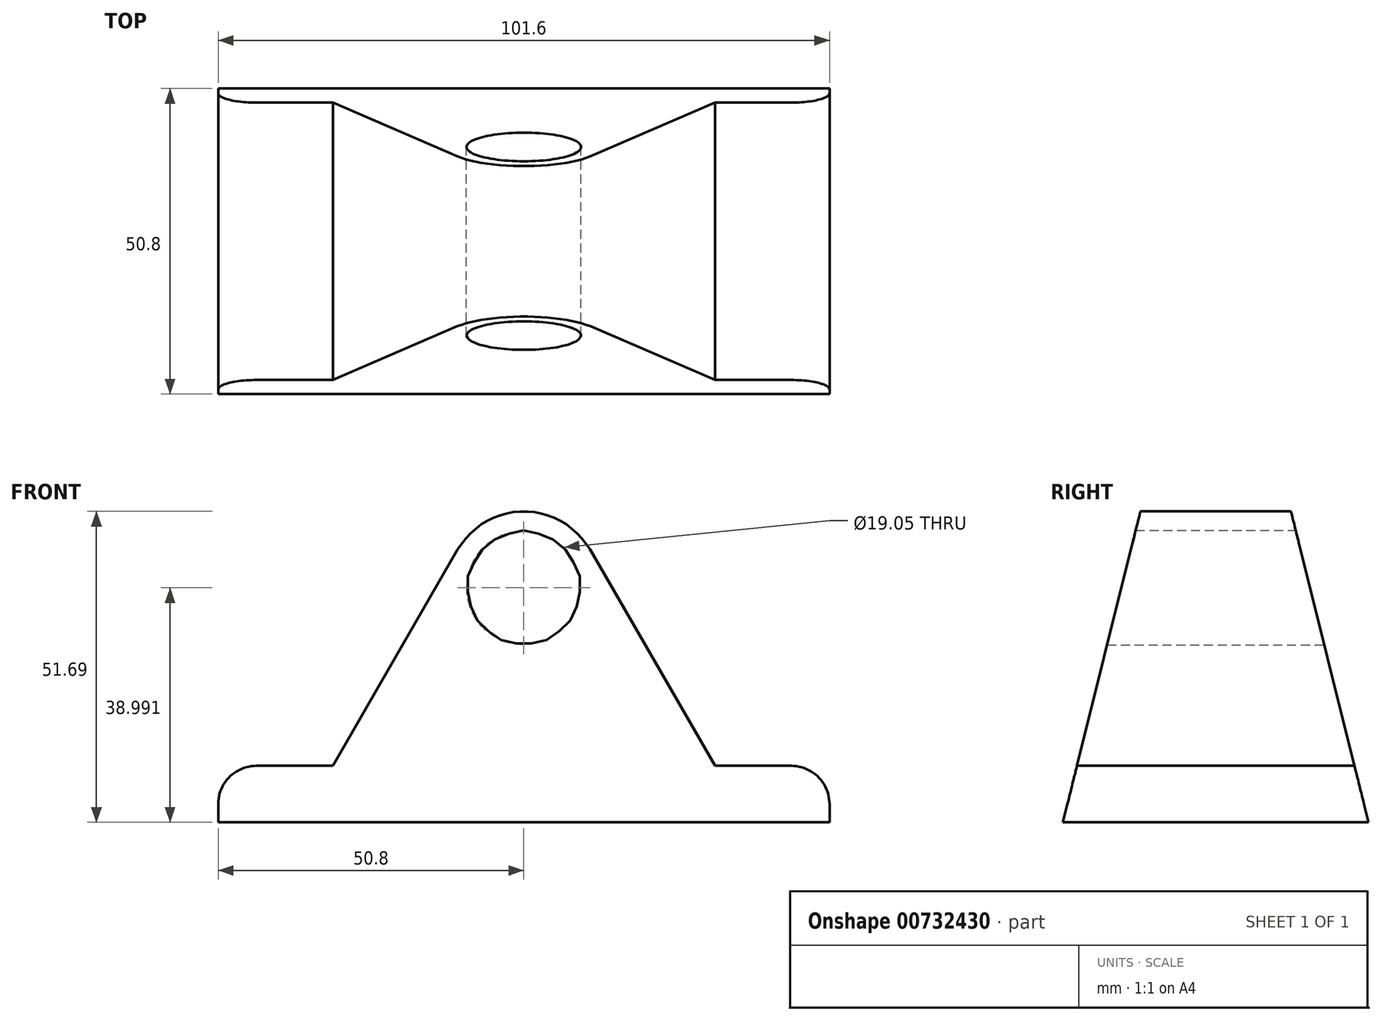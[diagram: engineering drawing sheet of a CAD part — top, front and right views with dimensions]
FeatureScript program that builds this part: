
annotation { "Feature Type Name" : "Feature", "Feature Type Description" : "" }
export const myFeature = defineFeature(function(context is Context, id is Id, definition is map)
    precondition{}
    {
        {
            var Q0;
            Q0=qCreatedBy(makeId("Front.planeOp"),FACE);
            var sketch = newSketch(context, id + "F0", { "sketchPlane" : qUnion([Q0])});
            skLineSegment(sketch, "E0", {"start": v(0, 0) * mm, "end": v(-50.8, 0) * mm});
            skLineSegment(sketch, "E1", {"start": v(-50.8, 0) * mm, "end": v(-50.8, 3.05) * mm});
            skLineSegment(sketch, "E2", {"start": v(-44.45, 9.4) * mm, "end": v(-31.75, 9.4) * mm});
            skLineSegment(sketch, "E3", {"start": v(-31.75, 9.4) * mm, "end": v(-11, 45.34) * mm});
            skLineSegment(sketch, "E4", {"start": v(11, 45.34) * mm, "end": v(31.75, 9.4) * mm});
            skLineSegment(sketch, "E5", {"start": v(31.75, 9.4) * mm, "end": v(44.45, 9.4) * mm});
            skLineSegment(sketch, "E6", {"start": v(50.8, 3.05) * mm, "end": v(50.8, 0) * mm});
            skLineSegment(sketch, "E7", {"start": v(50.8, 0) * mm, "end": v(0, 0) * mm});
            skPoint(sketch, "E8.visualSharp", {"position": v(0, 64.4) * mm});
            skArc(sketch, "E8.filletArc", {"start": v(11, 45.34) * mm, "mid": v(0, 51.7) * mm, "end": v(-11, 45.34) * mm});
            skPoint(sketch, "E9.visualSharp", {"position": v(-50.8, 9.4) * mm});
            skArc(sketch, "E9.filletArc", {"start": v(-44.45, 9.4) * mm, "mid": v(-48.94, 7.54) * mm, "end": v(-50.8, 3.05) * mm});
            skPoint(sketch, "E10.visualSharp", {"position": v(50.8, 9.4) * mm});
            skArc(sketch, "E10.filletArc", {"start": v(50.8, 3.05) * mm, "mid": v(48.94, 7.54) * mm, "end": v(44.45, 9.4) * mm});
            skCircle(sketch, "E11", {"center": v(0, 39) * mm, "radius": 9.53 * mm});
            skSolve(sketch);
        }
        {
            var Q0;
            Q0=makeQuery(id+"F0.imprint","IMPRINT",FACE,{"disambiguationData":[TD([[makeQuery(id+"F0.imprint","IMPRINT",EDGE,{"derivedFrom":sQuery(id+"F0.wireOp",EDGE,"E0")}),-1.0]])]});
            extrude(context, id + "F1", {"entities" : qUnion([Q0]), "endBound" : BoundingType.SYMMETRIC, "depth" : 50.8 * mm, "offsetDistance" : 25.4 * mm});
        }
        {
            var Q0;
            Q0=qCreatedBy(makeId("Right.planeOp"),FACE);
            var sketch = newSketch(context, id + "F2", { "sketchPlane" : qUnion([Q0])});
            skLineSegment(sketch, "E12", {"start": v(-10.2, 60.96) * mm, "end": v(-33.02, -30.56) * mm});
            skLineSegment(sketch, "E13", {"start": v(-33.02, -30.56) * mm, "end": v(-33.02, 60.96) * mm});
            skLineSegment(sketch, "E14", {"start": v(-33.02, 60.96) * mm, "end": v(-10.2, 60.96) * mm});
            skLineSegment(sketch, "E15.MirrorCS", {"start": v(33.02, -30.56) * mm, "end": v(33.02, 60.96) * mm});
            skLineSegment(sketch, "E16.MirrorCS", {"start": v(10.2, 60.96) * mm, "end": v(33.02, -30.56) * mm});
            skLineSegment(sketch, "E17.MirrorCS", {"start": v(33.02, 60.96) * mm, "end": v(10.2, 60.96) * mm});
            skLineSegment(sketch, "E18.0", {"start": v(-25.4, 3.05) * mm, "end": v(-25.4, 0) * mm});
            skSolve(sketch);
        }
        {
            var Q0;
            Q0=makeQuery(id+"F2.imprint","IMPRINT",FACE,{"disambiguationData":[TD([[makeQuery(id+"F2.imprint","IMPRINT",EDGE,{"derivedFrom":sQuery(id+"F2.wireOp",EDGE,"E12")}),-1.0]])]});
            var Q1;
            Q1=makeQuery(id+"F2.imprint","IMPRINT",FACE,{"disambiguationData":[TD([[makeQuery(id+"F2.imprint","IMPRINT",EDGE,{"derivedFrom":sQuery(id+"F2.wireOp",EDGE,"E15.MirrorCS")}),1.0]])]});
            extrude(context, id + "F3", {"entities" : qUnion([Q0, Q1]), "operationType" : NewBodyOperationType.REMOVE, "endBound" : BoundingType.SYMMETRIC, "depth" : 101.6 * mm, "offsetDistance" : 25.4 * mm});
        }
    });
